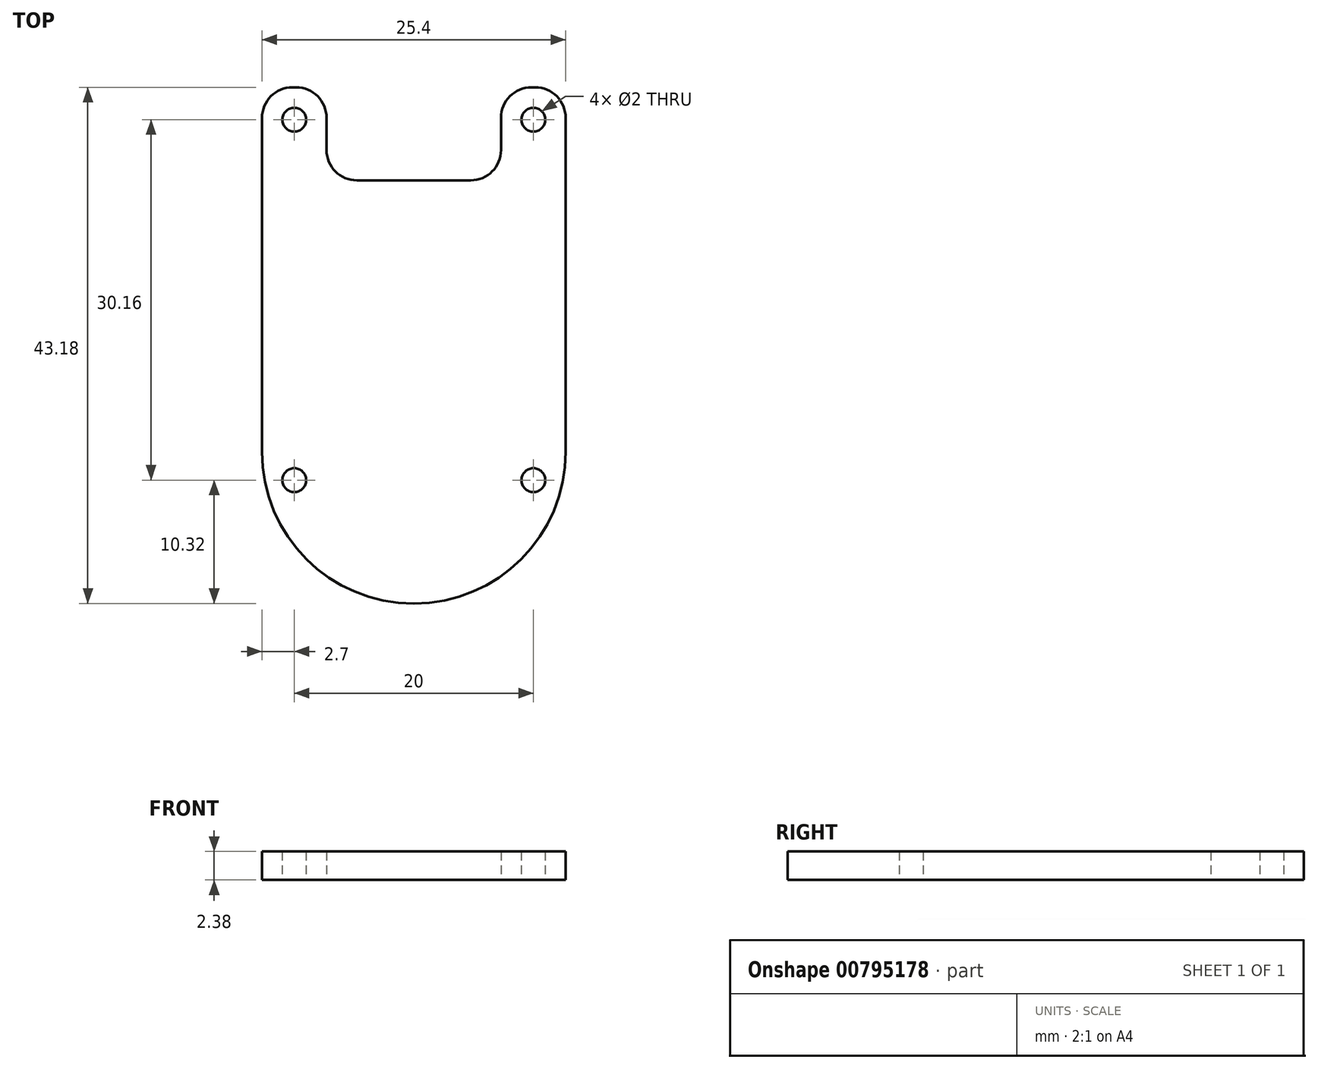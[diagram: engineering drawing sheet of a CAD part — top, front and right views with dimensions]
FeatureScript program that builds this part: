
annotation { "Feature Type Name" : "Feature", "Feature Type Description" : "" }
export const myFeature = defineFeature(function(context is Context, id is Id, definition is map)
    precondition{}
    {
        {
            var Q0;
            Q0=qCreatedBy(makeId("Top.planeOp"),FACE);
            var sketch = newSketch(context, id + "F0", { "sketchPlane" : qUnion([Q0])});
            skLineSegment(sketch, "E0", {"start": v(0, 0) * mm, "end": v(12.7, 0) * mm});
            skLineSegment(sketch, "E1", {"start": v(0, 0) * mm, "end": v(-12.7, 0) * mm});
            skLineSegment(sketch, "E2", {"start": v(12.7, 0) * mm, "end": v(12.7, -12.7) * mm});
            skLineSegment(sketch, "E3", {"start": v(-12.7, 0) * mm, "end": v(-12.7, -12.7) * mm});
            skLineSegment(sketch, "E4", {"start": v(0, -25.4) * mm, "end": v(0, -25.4) * mm});
            skLineSegment(sketch, "E5", {"start": v(-12.7, 0) * mm, "end": v(-12.7, 15.24) * mm});
            skLineSegment(sketch, "E6", {"start": v(12.7, 0) * mm, "end": v(12.7, 15.24) * mm});
            skLineSegment(sketch, "E7", {"start": v(10.16, 17.78) * mm, "end": v(-10.16, 17.78) * mm});
            skLineSegment(sketch, "E8.bottom", {"start": v(10, -10) * mm, "end": v(-10, -10) * mm});
            skLineSegment(sketch, "E8.top", {"start": v(4.76, 10) * mm, "end": v(-4.76, 10) * mm});
            skLineSegment(sketch, "E8.left", {"start": v(10, -10) * mm, "end": v(10, 10) * mm});
            skLineSegment(sketch, "E8.right", {"start": v(-10, -10) * mm, "end": v(-10, 10) * mm});
            skPoint(sketch, "E8.middle", {"position": v(0, 0) * mm});
            skPoint(sketch, "E9.visualSharp", {"position": v(-12.7, -25.4) * mm});
            skArc(sketch, "E9.filletArc", {"start": v(-12.7, -12.7) * mm, "mid": v(-8.98, -21.68) * mm, "end": v(0, -25.4) * mm});
            skPoint(sketch, "E10.visualSharp", {"position": v(12.7, -25.4) * mm});
            skArc(sketch, "E10.filletArc", {"start": v(0, -25.4) * mm, "mid": v(8.98, -21.68) * mm, "end": v(12.7, -12.7) * mm});
            skLineSegment(sketch, "E11", {"start": v(10, 10) * mm, "end": v(10, 15.08) * mm});
            skLineSegment(sketch, "E12", {"start": v(-10, 10) * mm, "end": v(-10, 15.08) * mm});
            skCircle(sketch, "E13", {"center": v(-10, 15.08) * mm, "radius": 1 * mm});
            skCircle(sketch, "E14", {"center": v(10, 15.08) * mm, "radius": 1 * mm});
            skLineSegment(sketch, "E15", {"start": v(10, 15.08) * mm, "end": v(9, 15.08) * mm});
            skLineSegment(sketch, "E16", {"start": v(9, 15.08) * mm, "end": v(7.3, 15.08) * mm});
            skLineSegment(sketch, "E17", {"start": v(7.3, 15.08) * mm, "end": v(7.3, 17.78) * mm});
            skLineSegment(sketch, "E18", {"start": v(-10, 15.08) * mm, "end": v(-9, 15.08) * mm});
            skLineSegment(sketch, "E19", {"start": v(-9, 15.08) * mm, "end": v(-7.3, 15.08) * mm});
            skLineSegment(sketch, "E20", {"start": v(-7.3, 15.08) * mm, "end": v(-7.3, 15.24) * mm});
            skLineSegment(sketch, "E21", {"start": v(7.3, 15.24) * mm, "end": v(7.3, 12.54) * mm});
            skLineSegment(sketch, "E22", {"start": v(-7.3, 17.78) * mm, "end": v(-7.3, 12.54) * mm});
            skPoint(sketch, "E23.visualSharp", {"position": v(-12.7, 17.78) * mm});
            skArc(sketch, "E23.filletArc", {"start": v(-10.16, 17.78) * mm, "mid": v(-11.96, 17.04) * mm, "end": v(-12.7, 15.24) * mm});
            skPoint(sketch, "E24.visualSharp", {"position": v(12.7, 17.78) * mm});
            skArc(sketch, "E24.filletArc", {"start": v(12.7, 15.24) * mm, "mid": v(11.96, 17.04) * mm, "end": v(10.16, 17.78) * mm});
            skPoint(sketch, "E25", {"position": v(-9.51, 17.78) * mm});
            skPoint(sketch, "E26", {"position": v(9.28, 17.78) * mm});
            skLineSegment(sketch, "E27", {"start": v(-9.84, 17.78) * mm, "end": v(-10.16, 17.78) * mm});
            skLineSegment(sketch, "E28", {"start": v(0, 17.78) * mm, "end": v(10.16, 17.78) * mm});
            skPoint(sketch, "E29.newPointA", {"position": v(0, 17.78) * mm});
            skArc(sketch, "E29.filletArc", {"start": v(-7.3, 15.24) * mm, "mid": v(-8.04, 17.04) * mm, "end": v(-9.84, 17.78) * mm});
            skLineSegment(sketch, "E30", {"start": v(9.84, 17.78) * mm, "end": v(10.16, 17.78) * mm});
            skPoint(sketch, "E31.visualSharp", {"position": v(7.3, 17.78) * mm});
            skArc(sketch, "E31.filletArc", {"start": v(9.84, 17.78) * mm, "mid": v(8.04, 17.04) * mm, "end": v(7.3, 15.24) * mm});
            skPoint(sketch, "E32.newPointB", {"position": v(-10, 10) * mm});
            skArc(sketch, "E32.filletArc", {"start": v(-7.3, 12.54) * mm, "mid": v(-6.55, 10.74) * mm, "end": v(-4.76, 10) * mm});
            skPoint(sketch, "E33.newPointB", {"position": v(10, 10) * mm});
            skArc(sketch, "E33.filletArc", {"start": v(4.76, 10) * mm, "mid": v(6.55, 10.74) * mm, "end": v(7.3, 12.54) * mm});
            skLineSegment(sketch, "E34", {"start": v(10, -10) * mm, "end": v(10, -15.08) * mm});
            skCircle(sketch, "E35", {"center": v(10, -15.08) * mm, "radius": 1 * mm});
            skLineSegment(sketch, "E36", {"start": v(-10, -10) * mm, "end": v(-10, -15.08) * mm});
            skCircle(sketch, "E37", {"center": v(-10, -15.08) * mm, "radius": 1 * mm});
            skSolve(sketch);
        }
        {
            var Q0;
            {var subQ1=sQuery(id+"F0.wireOp",EDGE,"E8.bottom");Q0=makeQuery(id+"F0.imprint","IMPRINT",FACE,{"disambiguationData":[TD([[makeQuery(id+"F0.imprint","IMPRINT",EDGE,{"derivedFrom":subQ1}),-1.0]])]});}
            var Q1;
            {var subQ5=sQuery(id+"F0.wireOp",EDGE,"E6");Q1=makeQuery(id+"F0.imprint","IMPRINT",FACE,{"disambiguationData":[TD([[makeQuery(id+"F0.imprint","IMPRINT",EDGE,{"derivedFrom":subQ5}),1.0]])]});}
            var Q2;
            Q2=makeQuery(id+"F0.imprint","IMPRINT",FACE,{"disambiguationData":[TD([[makeQuery(id+"F0.imprint","IMPRINT",EDGE,{"derivedFrom":sQuery(id+"F0.wireOp",EDGE,"E8.top")}),1.0]])]});
            var Q3;
            {var subQ7=sQuery(id+"F0.wireOp",EDGE,"E5");Q3=makeQuery(id+"F0.imprint","IMPRINT",FACE,{"disambiguationData":[TD([[makeQuery(id+"F0.imprint","IMPRINT",EDGE,{"derivedFrom":subQ7}),-1.0]])]});}
            var Q4;
            {var subQ4=sQuery(id+"F0.wireOp",EDGE,"E2");Q4=makeQuery(id+"F0.imprint","IMPRINT",FACE,{"disambiguationData":[TD([[makeQuery(id+"F0.imprint","IMPRINT",EDGE,{"derivedFrom":subQ4}),-1.0]])]});}
            extrude(context, id + "F1", {"entities" : qUnion([Q0, Q1, Q2, Q3, Q4]), "depth" : 2.38 * mm, "offsetDistance" : 25.4 * mm});
        }
    });
